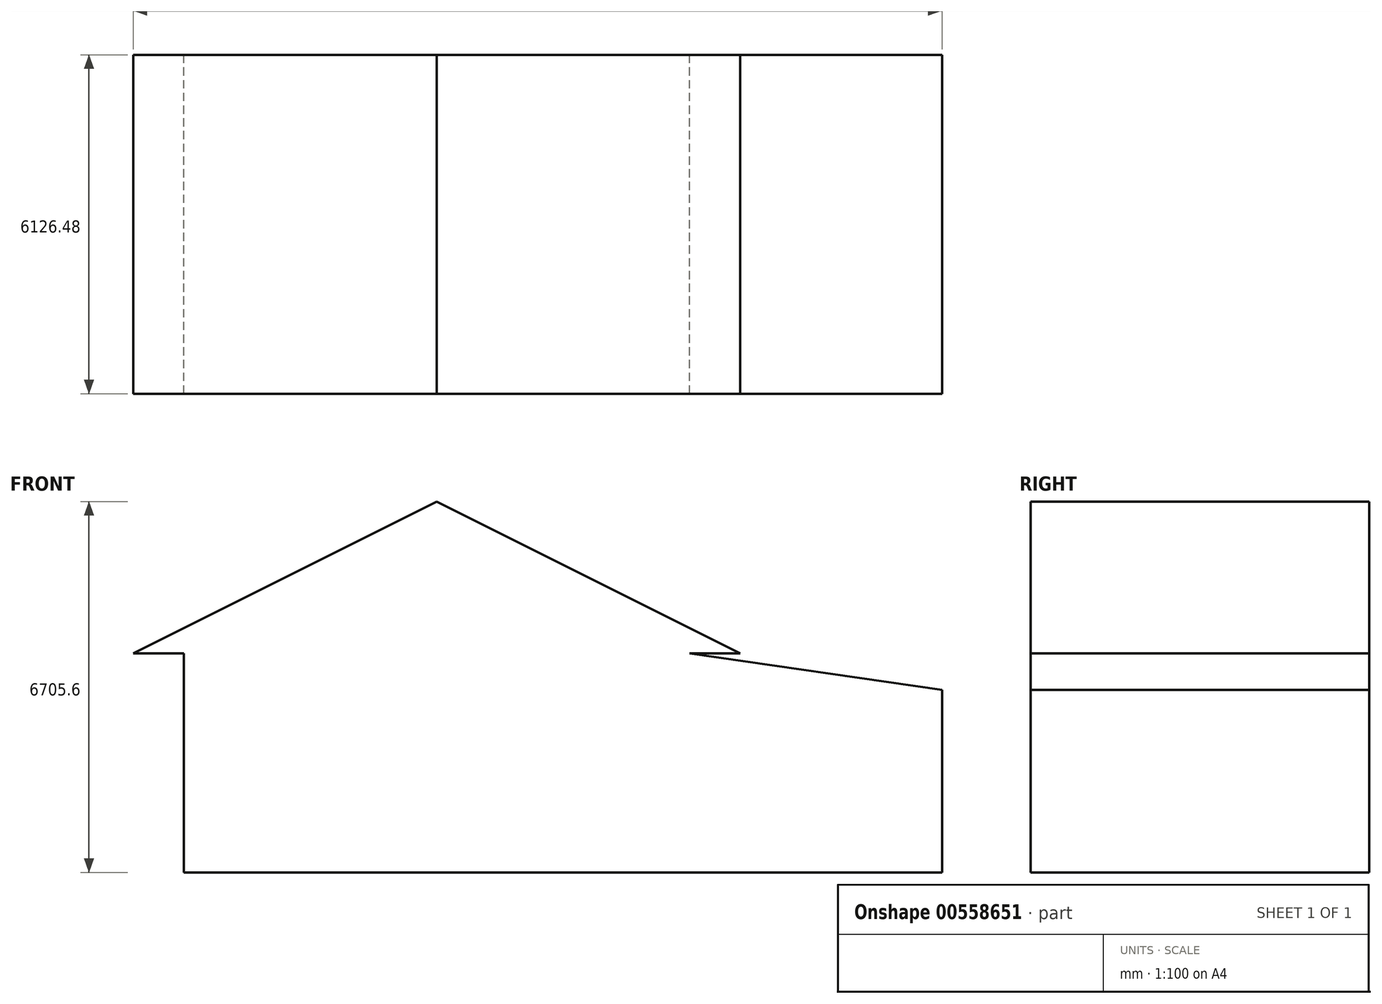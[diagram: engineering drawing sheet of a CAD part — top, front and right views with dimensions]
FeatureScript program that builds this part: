
annotation { "Feature Type Name" : "Feature", "Feature Type Description" : "" }
export const myFeature = defineFeature(function(context is Context, id is Id, definition is map)
    precondition{}
    {
        {
            var Q0;
            Q0=qCreatedBy(makeId("Front.planeOp"),FACE);
            var sketch = newSketch(context, id + "F0", { "sketchPlane" : qUnion([Q0])});
            skLineSegment(sketch, "E0", {"start": v(0, 0) * mm, "end": v(-4572, 0) * mm});
            skLineSegment(sketch, "E1", {"start": v(0, 0) * mm, "end": v(4572, 0) * mm});
            skLineSegment(sketch, "E2", {"start": v(0, 0) * mm, "end": v(0, 2286) * mm});
            skLineSegment(sketch, "E3", {"start": v(0, 2286) * mm, "end": v(0, 2743.2) * mm});
            skLineSegment(sketch, "E4", {"start": v(-4572, 0) * mm, "end": v(-5486.4, 0) * mm});
            skLineSegment(sketch, "E5", {"start": v(4572, 0) * mm, "end": v(5486.4, 0) * mm});
            skLineSegment(sketch, "E6", {"start": v(5486.4, 0) * mm, "end": v(0, 2743.2) * mm});
            skLineSegment(sketch, "E7", {"start": v(-5486.4, 0) * mm, "end": v(0, 2743.2) * mm});
            skLineSegment(sketch, "E8", {"start": v(-4572, 0) * mm, "end": v(0, 2286) * mm});
            skLineSegment(sketch, "E9", {"start": v(4572, 0) * mm, "end": v(0, 2286) * mm});
            skLineSegment(sketch, "E10", {"start": v(-4572, 0) * mm, "end": v(-4572, -3352.8) * mm});
            skLineSegment(sketch, "E11", {"start": v(4572, 0) * mm, "end": v(4572, -3352.8) * mm});
            skLineSegment(sketch, "E12", {"start": v(-4572, -3352.8) * mm, "end": v(4572, -3352.8) * mm});
            skLineSegment(sketch, "E13", {"start": v(-4572, -3352.8) * mm, "end": v(-4572, -3962.4) * mm});
            skLineSegment(sketch, "E14", {"start": v(4572, -3352.8) * mm, "end": v(4572, -3962.4) * mm});
            skLineSegment(sketch, "E15", {"start": v(-4572, -3962.4) * mm, "end": v(4572, -3962.4) * mm});
            skLineSegment(sketch, "E16", {"start": v(-3352.8, -3352.8) * mm, "end": v(-3352.8, -1219.2) * mm});
            skLineSegment(sketch, "E17", {"start": v(-3352.8, -1219.2) * mm, "end": v(-2438.4, -1219.2) * mm});
            skLineSegment(sketch, "E18", {"start": v(-2438.4, -1219.2) * mm, "end": v(-2438.4, -3352.8) * mm});
            skLineSegment(sketch, "E19", {"start": v(-3352.8, -1219.2) * mm, "end": v(-4572, -1219.2) * mm, "construction": true});
            skLineSegment(sketch, "E20", {"start": v(4572, -1219.2) * mm, "end": v(3352.8, -1219.2) * mm, "construction": true});
            skPoint(sketch, "E20.startSnap0", {"position": v(4572, -1676.4) * mm});
            skLineSegment(sketch, "E21", {"start": v(3352.8, -673.97) * mm, "end": v(3352.8, -2045.57) * mm});
            skLineSegment(sketch, "E22", {"start": v(3352.8, -2045.57) * mm, "end": v(609.6, -2045.57) * mm});
            skLineSegment(sketch, "E23", {"start": v(609.6, -2045.57) * mm, "end": v(609.6, -673.97) * mm});
            skLineSegment(sketch, "E24", {"start": v(3352.8, -673.97) * mm, "end": v(609.6, -673.97) * mm});
            skLineSegment(sketch, "E25", {"start": v(4572, 0) * mm, "end": v(9135.8, -662.4) * mm});
            skLineSegment(sketch, "E26", {"start": v(4572, -401.15) * mm, "end": v(9135.8, -1063.54) * mm});
            skLineSegment(sketch, "E27", {"start": v(9135.8, -662.4) * mm, "end": v(9135.8, -1063.54) * mm});
            skLineSegment(sketch, "E28", {"start": v(4572, -3352.8) * mm, "end": v(9135.8, -3352.8) * mm});
            skLineSegment(sketch, "E29", {"start": v(9135.8, -1063.54) * mm, "end": v(9135.8, -3352.8) * mm});
            skLineSegment(sketch, "E30", {"start": v(4572, -3962.4) * mm, "end": v(9135.8, -3962.4) * mm});
            skLineSegment(sketch, "E31", {"start": v(9135.8, -3352.8) * mm, "end": v(9135.8, -3962.4) * mm});
            skLineSegment(sketch, "E32", {"start": v(4572, -2273.3) * mm, "end": v(5791.2, -2273.3) * mm, "construction": true});
            skLineSegment(sketch, "E33", {"start": v(5739.97, -1829.66) * mm, "end": v(5791.2, -3352.8) * mm, "construction": true});
            skPoint(sketch, "E34.oppositeSnap0", {"position": v(5765.59, -2591.23) * mm});
            skLineSegment(sketch, "E34.bottom", {"start": v(5739.97, -1829.66) * mm, "end": v(6959.17, -1829.66) * mm});
            skLineSegment(sketch, "E34.top", {"start": v(5739.97, -2591.23) * mm, "end": v(6959.17, -2591.23) * mm});
            skLineSegment(sketch, "E34.left", {"start": v(5739.97, -1829.66) * mm, "end": v(5739.97, -2591.23) * mm});
            skLineSegment(sketch, "E34.right", {"start": v(6959.17, -1829.66) * mm, "end": v(6959.17, -2591.23) * mm});
            skSolve(sketch);
        }
        {
            var Q0;
            Q0=makeQuery(id+"F0.imprint","IMPRINT",FACE,{"disambiguationData":[TD([[makeQuery(id+"F0.imprint","IMPRINT",EDGE,{"derivedFrom":sQuery(id+"F0.wireOp",EDGE,"E21")}),-1.0]])]});
            var Q1;
            Q1=makeQuery(id+"F0.imprint","IMPRINT",FACE,{"disambiguationData":[TD([[makeQuery(id+"F0.imprint","IMPRINT",EDGE,{"derivedFrom":sQuery(id+"F0.wireOp",EDGE,"E34.bottom")}),-1.0]])]});
            var Q2;
            Q2=makeQuery(id+"F0.imprint","IMPRINT",FACE,{"disambiguationData":[TD([[makeQuery(id+"F0.imprint","IMPRINT",EDGE,{"derivedFrom":sQuery(id+"F0.wireOp",EDGE,"E3")}),1.0]])]});
            var Q3;
            Q3=makeQuery(id+"F0.imprint","IMPRINT",FACE,{"disambiguationData":[TD([[makeQuery(id+"F0.imprint","IMPRINT",EDGE,{"derivedFrom":sQuery(id+"F0.wireOp",EDGE,"E3")}),-1.0]])]});
            var Q4;
            {var subQ0=sQuery(id+"F0.wireOp",EDGE,"E25");Q4=makeQuery(id+"F0.imprint","IMPRINT",FACE,{"disambiguationData":[TD([[makeQuery(id+"F0.imprint","IMPRINT",EDGE,{"derivedFrom":subQ0}),-1.0]])]});}
            var Q5;
            {var subQ0=sQuery(id+"F0.wireOp",EDGE,"E16");Q5=makeQuery(id+"F0.imprint","IMPRINT",FACE,{"disambiguationData":[TD([[makeQuery(id+"F0.imprint","IMPRINT",EDGE,{"derivedFrom":subQ0}),-1.0]])]});}
            var Q6;
            Q6=makeQuery(id+"F0.imprint","IMPRINT",FACE,{"disambiguationData":[TD([[makeQuery(id+"F0.imprint","IMPRINT",EDGE,{"derivedFrom":sQuery(id+"F0.wireOp",EDGE,"E14")}),1.0]])]});
            var Q7;
            Q7=makeQuery(id+"F0.imprint","IMPRINT",FACE,{"disambiguationData":[TD([[makeQuery(id+"F0.imprint","IMPRINT",EDGE,{"derivedFrom":sQuery(id+"F0.wireOp",EDGE,"E0")}),-1.0]])]});
            var Q8;
            Q8=makeQuery(id+"F0.imprint","IMPRINT",FACE,{"disambiguationData":[TD([[makeQuery(id+"F0.imprint","IMPRINT",EDGE,{"derivedFrom":sQuery(id+"F0.wireOp",EDGE,"E1")}),1.0]])]});
            var Q9;
            {var subQ0=sQuery(id+"F0.wireOp",EDGE,"E13");Q9=makeQuery(id+"F0.imprint","IMPRINT",FACE,{"disambiguationData":[TD([[makeQuery(id+"F0.imprint","IMPRINT",EDGE,{"derivedFrom":subQ0}),1.0]])]});}
            var Q10;
            {var subQ1=sQuery(id+"F0.wireOp",EDGE,"E26");Q10=makeQuery(id+"F0.imprint","IMPRINT",FACE,{"disambiguationData":[TD([[makeQuery(id+"F0.imprint","IMPRINT",EDGE,{"derivedFrom":subQ1}),-1.0]])]});}
            var Q11;
            Q11=makeQuery(id+"F0.imprint","IMPRINT",FACE,{"disambiguationData":[TD([[makeQuery(id+"F0.imprint","IMPRINT",EDGE,{"derivedFrom":sQuery(id+"F0.wireOp",EDGE,"E0")}),1.0]])]});
            extrude(context, id + "F1", {"entities" : qUnion([Q0, Q1, Q2, Q3, Q4, Q5, Q6, Q7, Q8, Q9, Q10, Q11]), "depth" : 6096 * mm, "offsetDistance" : 30.48 * mm, "hasSecondDirection" : true, "secondDirectionOppositeDirection" : true, "secondDirectionDepth" : 30.48 * mm});
        }
        {
            var Q0;
            Q0=sQuery(id+"F0.wireOp",EDGE,"E18");
            var Q1;
            Q1=sQuery(id+"F0.wireOp",EDGE,"E17");
            var Q2;
            Q2=sQuery(id+"F0.wireOp",EDGE,"E16");
            extrude(context, id + "F2", {"bodyType" : ToolBodyType.SURFACE, "surfaceEntities" : qUnion([Q0, Q1, Q2]), "depth" : 304.8 * mm, "offsetDistance" : 30.48 * mm});
        }
        {
            var Q0;
            Q0=sQuery(id+"F0.wireOp",EDGE,"E16");
            var Q1;
            Q1=sQuery(id+"F0.wireOp",EDGE,"E17");
            var Q2;
            Q2=sQuery(id+"F0.wireOp",EDGE,"E18");
            extrude(context, id + "F3", {"bodyType" : ToolBodyType.SURFACE, "surfaceEntities" : qUnion([Q0, Q1, Q2]), "depth" : 304.8 * mm, "offsetDistance" : 30.48 * mm, "hasSecondDirection" : true, "secondDirectionOppositeDirection" : true, "secondDirectionDepth" : 304.8 * mm});
        }
        {
            var Q0;
            Q0=sQuery(id+"F0.wireOp",EDGE,"E17");
            var Q1;
            Q1=sQuery(id+"F0.wireOp",EDGE,"E16");
            var Q2;
            Q2=sQuery(id+"F0.wireOp",EDGE,"E18");
            extrude(context, id + "F4", {"bodyType" : ToolBodyType.SURFACE, "surfaceEntities" : qUnion([Q0, Q1, Q2]), "oppositeDirection" : true, "depth" : 304.8 * mm, "offsetDistance" : 30.48 * mm});
        }
    });
